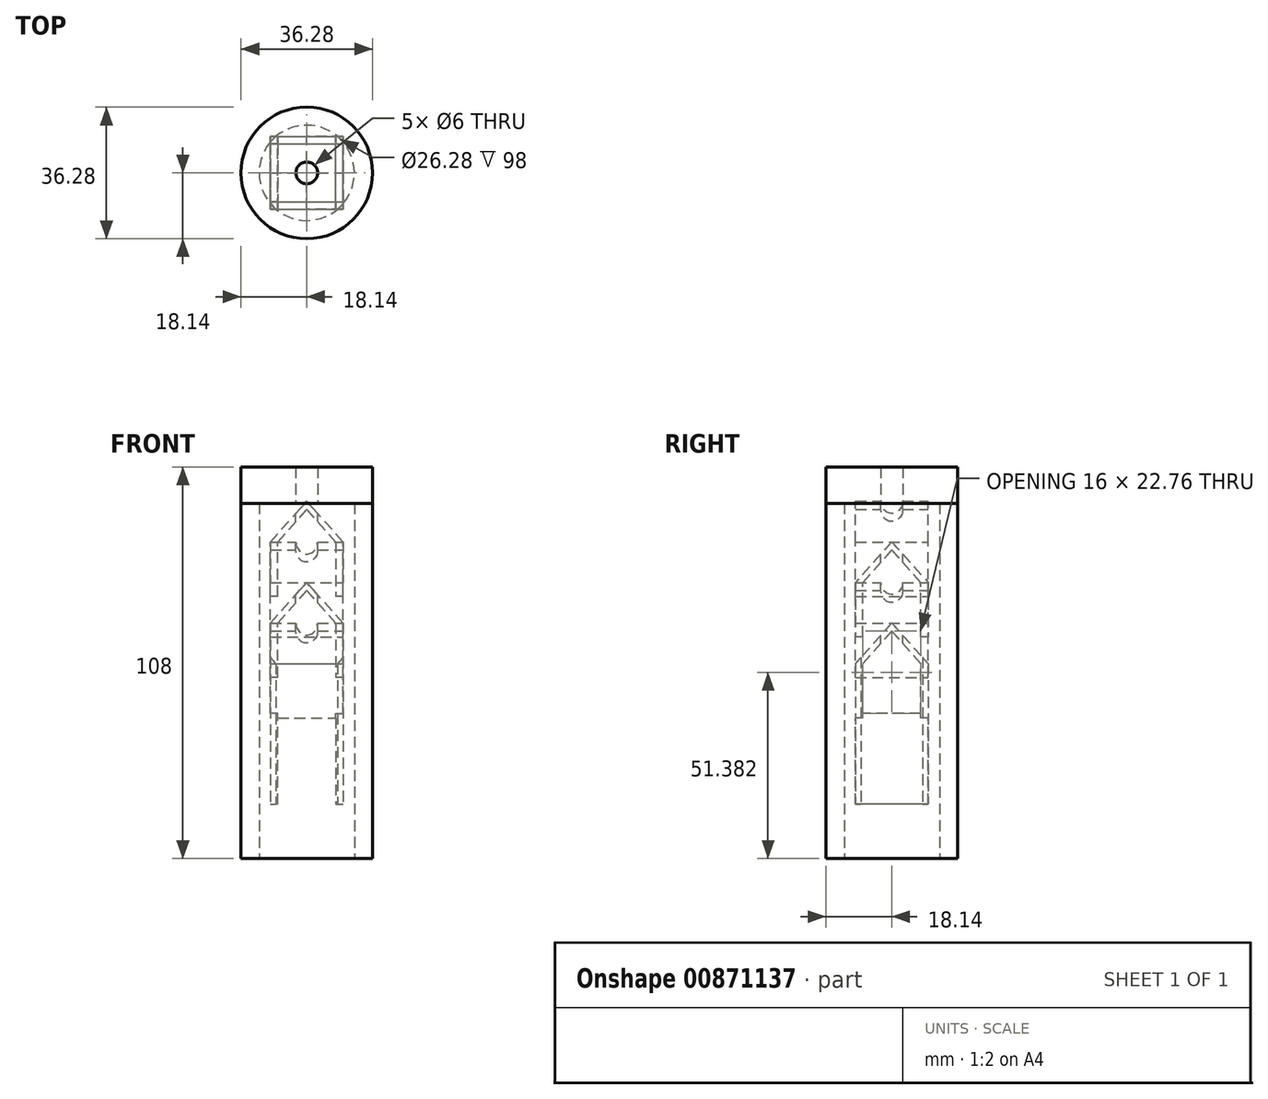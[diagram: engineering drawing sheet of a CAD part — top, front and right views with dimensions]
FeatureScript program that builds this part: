
annotation { "Feature Type Name" : "Feature", "Feature Type Description" : "" }
export const myFeature = defineFeature(function(context is Context, id is Id, definition is map)
    precondition{}
    {
        {
            var Q0;
            Q0=qCreatedBy(makeId("Front.planeOp"),FACE);
            var sketch = newSketch(context, id + "F0", { "sketchPlane" : qUnion([Q0])});
            skLineSegment(sketch, "E0", {"start": v(-10, 0) * mm, "end": v(-10, 15) * mm});
            skLineSegment(sketch, "E1", {"start": v(-10, 15) * mm, "end": v(0, 26.18) * mm});
            skLineSegment(sketch, "E2", {"start": v(0, 0) * mm, "end": v(0, 43.3) * mm, "construction": true});
            skLineSegment(sketch, "E3.MirrorCS", {"start": v(10, 15) * mm, "end": v(0, 26.18) * mm});
            skLineSegment(sketch, "E4.MirrorCS", {"start": v(10, 0) * mm, "end": v(10, 15) * mm});
            skLineSegment(sketch, "E5", {"start": v(-8, 0) * mm, "end": v(-8, 15) * mm});
            skLineSegment(sketch, "E6", {"start": v(-8, 15) * mm, "end": v(0, 23.94) * mm});
            skLineSegment(sketch, "E7", {"start": v(0, 23.94) * mm, "end": v(8, 15) * mm});
            skLineSegment(sketch, "E8", {"start": v(8, 15) * mm, "end": v(8, 0) * mm});
            skLineSegment(sketch, "E9", {"start": v(10, 15) * mm, "end": v(-10, 15) * mm, "construction": true});
            skLineSegment(sketch, "E10", {"start": v(10, 0) * mm, "end": v(8, 0) * mm});
            skLineSegment(sketch, "E11", {"start": v(-8, 0) * mm, "end": v(-10, 0) * mm});
            skLineSegment(sketch, "E12.1.0.0", {"start": v(-8, -7.36) * mm, "end": v(0, 1.58) * mm});
            skLineSegment(sketch, "E12.1.0.1", {"start": v(-10, -7.36) * mm, "end": v(0, 3.82) * mm});
            skLineSegment(sketch, "E12.1.0.2", {"start": v(10, -7.36) * mm, "end": v(0, 3.82) * mm});
            skLineSegment(sketch, "E12.1.0.3", {"start": v(0, 1.58) * mm, "end": v(8, -7.36) * mm});
            skLineSegment(sketch, "E12.1.0.4", {"start": v(8, -7.36) * mm, "end": v(8, -22.36) * mm});
            skLineSegment(sketch, "E12.1.0.5", {"start": v(10, -22.36) * mm, "end": v(10, -7.36) * mm});
            skLineSegment(sketch, "E12.1.0.6", {"start": v(-8, -22.36) * mm, "end": v(-8, -7.36) * mm});
            skLineSegment(sketch, "E12.1.0.7", {"start": v(-10, -22.36) * mm, "end": v(-10, -7.36) * mm});
            skLineSegment(sketch, "E12.1.0.8", {"start": v(-8, -22.36) * mm, "end": v(-10, -22.36) * mm});
            skLineSegment(sketch, "E12.1.0.9", {"start": v(10, -22.36) * mm, "end": v(8, -22.36) * mm});
            skLineSegment(sketch, "E12.direction1", {"start": v(-8, 15) * mm, "end": v(-8, -13.7) * mm, "construction": true});
            skLineSegment(sketch, "E13", {"start": v(-10, -22.36) * mm, "end": v(10, -22.36) * mm, "construction": true});
            skSolve(sketch);
        }
        {
            var Q0;
            Q0=qCreatedBy(makeId("Right.planeOp"),FACE);
            var sketch = newSketch(context, id + "F1", { "sketchPlane" : qUnion([Q0])});
            skLineSegment(sketch, "E14", {"start": v(0, 15) * mm, "end": v(-10, 3.82) * mm});
            skLineSegment(sketch, "E15", {"start": v(-10, 3.82) * mm, "end": v(-10, -11.18) * mm});
            skLineSegment(sketch, "E16", {"start": v(-8, -11.18) * mm, "end": v(-8, 3.82) * mm});
            skLineSegment(sketch, "E17", {"start": v(-8, 3.82) * mm, "end": v(0, 12.76) * mm});
            skLineSegment(sketch, "E18.MirrorCS", {"start": v(8, 3.82) * mm, "end": v(0, 12.76) * mm});
            skLineSegment(sketch, "E19.MirrorCS", {"start": v(0, 15) * mm, "end": v(10, 3.82) * mm});
            skLineSegment(sketch, "E20.MirrorCS", {"start": v(8, -11.18) * mm, "end": v(8, 3.82) * mm});
            skLineSegment(sketch, "E21.MirrorCS", {"start": v(10, 3.82) * mm, "end": v(10, -11.18) * mm});
            skLineSegment(sketch, "E22", {"start": v(10, 3.82) * mm, "end": v(-10, 3.82) * mm, "construction": true});
            skLineSegment(sketch, "E23", {"start": v(10, -11.18) * mm, "end": v(8, -11.18) * mm});
            skLineSegment(sketch, "E24", {"start": v(-8, -11.18) * mm, "end": v(-10, -11.18) * mm});
            skLineSegment(sketch, "E25.1.0.0", {"start": v(0, -7.36) * mm, "end": v(10, -18.54) * mm});
            skLineSegment(sketch, "E25.1.0.1", {"start": v(8, -18.54) * mm, "end": v(0, -9.6) * mm});
            skLineSegment(sketch, "E25.1.0.2", {"start": v(8, -33.54) * mm, "end": v(8, -18.54) * mm});
            skLineSegment(sketch, "E25.1.0.3", {"start": v(10, -18.54) * mm, "end": v(10, -33.54) * mm});
            skLineSegment(sketch, "E25.1.0.4", {"start": v(10, -33.54) * mm, "end": v(8, -33.54) * mm});
            skLineSegment(sketch, "E25.1.0.5", {"start": v(-8, -33.54) * mm, "end": v(-10, -33.54) * mm});
            skLineSegment(sketch, "E25.1.0.6", {"start": v(-8, -33.54) * mm, "end": v(-8, -18.54) * mm});
            skLineSegment(sketch, "E25.1.0.7", {"start": v(-10, -18.54) * mm, "end": v(-10, -33.54) * mm});
            skLineSegment(sketch, "E25.1.0.8", {"start": v(0, -7.36) * mm, "end": v(-10, -18.54) * mm});
            skLineSegment(sketch, "E25.1.0.9", {"start": v(-8, -18.54) * mm, "end": v(0, -9.6) * mm});
            skLineSegment(sketch, "E25.direction1", {"start": v(10, 3.82) * mm, "end": v(10, -18.54) * mm, "construction": true});
            skSolve(sketch);
        }
        {
            var Q0;
            Q0=makeQuery(id+"F0.imprint","IMPRINT",FACE,{"disambiguationData":[TD([[makeQuery(id+"F0.imprint","IMPRINT",EDGE,{"derivedFrom":sQuery(id+"F0.wireOp",EDGE,"E0")}),-1.0]])]});
            var Q1;
            Q1=makeQuery(id+"F0.imprint","IMPRINT",FACE,{"disambiguationData":[TD([[makeQuery(id+"F0.imprint","IMPRINT",EDGE,{"derivedFrom":sQuery(id+"F0.wireOp",EDGE,"E12.1.0.0")}),1.0]])]});
            extrude(context, id + "F2", {"entities" : qUnion([Q0, Q1]), "endBound" : BoundingType.SYMMETRIC, "depth" : 20 * mm, "offsetDistance" : 25 * mm});
        }
        {
            var Q0;
            Q0 = qSketchRegion(id + "F1", true);
            extrude(context, id + "F3", {"entities" : qUnion([Q0]), "endBound" : BoundingType.SYMMETRIC, "oppositeDirection" : true, "depth" : 20 * mm, "offsetDistance" : 25 * mm});
        }
        {
            var Q0;
            Q0=makeQuery(id+"F3.opExtrude","CAP_FACE",FACE,{"disambiguationData":[OSD([sQuery(id+"F1.wireOp",EDGE,"E25.1.0.0"),sQuery(id+"F1.wireOp",EDGE,"E25.1.0.1"),sQuery(id+"F1.wireOp",EDGE,"E25.1.0.2"),sQuery(id+"F1.wireOp",EDGE,"E25.1.0.3"),sQuery(id+"F1.wireOp",EDGE,"E25.1.0.4"),sQuery(id+"F1.wireOp",EDGE,"E25.1.0.5"),sQuery(id+"F1.wireOp",EDGE,"E25.1.0.6"),sQuery(id+"F1.wireOp",EDGE,"E25.1.0.7"),sQuery(id+"F1.wireOp",EDGE,"E25.1.0.8"),sQuery(id+"F1.wireOp",EDGE,"E25.1.0.9")])],"isStart":true});
            var sketch = newSketch(context, id + "F4", { "sketchPlane" : qUnion([Q0])});
            skLineSegment(sketch, "E26", {"start": v(-10, -32.36) * mm, "end": v(10, -32.36) * mm});
            skLineSegment(sketch, "E27", {"start": v(-10, -32.36) * mm, "end": v(-10, -57.36) * mm});
            skLineSegment(sketch, "E28", {"start": v(-10, -57.36) * mm, "end": v(10, -57.36) * mm});
            skLineSegment(sketch, "E29", {"start": v(10, -57.36) * mm, "end": v(10, -32.36) * mm});
            skSolve(sketch);
        }
        {
            var Q0;
            Q0=makeQuery(id+"F3.opExtrude","CAP_FACE",FACE,{"disambiguationData":[OSD([sQuery(id+"F1.wireOp",EDGE,"E25.1.0.0"),sQuery(id+"F1.wireOp",EDGE,"E25.1.0.1"),sQuery(id+"F1.wireOp",EDGE,"E25.1.0.2"),sQuery(id+"F1.wireOp",EDGE,"E25.1.0.3"),sQuery(id+"F1.wireOp",EDGE,"E25.1.0.4"),sQuery(id+"F1.wireOp",EDGE,"E25.1.0.5"),sQuery(id+"F1.wireOp",EDGE,"E25.1.0.6"),sQuery(id+"F1.wireOp",EDGE,"E25.1.0.7"),sQuery(id+"F1.wireOp",EDGE,"E25.1.0.8"),sQuery(id+"F1.wireOp",EDGE,"E25.1.0.9")])],"isStart":false});
            var sketch = newSketch(context, id + "F5", { "sketchPlane" : qUnion([Q0])});
            skLineSegment(sketch, "E30", {"start": v(-10, -32.36) * mm, "end": v(10, -32.36) * mm});
            skLineSegment(sketch, "E31", {"start": v(-10, -32.36) * mm, "end": v(-10, -57.36) * mm});
            skLineSegment(sketch, "E32", {"start": v(-10, -57.36) * mm, "end": v(10, -57.36) * mm});
            skLineSegment(sketch, "E33", {"start": v(10, -57.36) * mm, "end": v(10, -32.36) * mm});
            skSolve(sketch);
        }
        {
            var Q0;
            {var subQ0=sQuery(id+"F5.wireOp",EDGE,"E32");Q0=makeQuery(id+"F5.imprint","IMPRINT",FACE,{"disambiguationData":[TD([[makeQuery(id+"F5.imprint","IMPRINT",EDGE,{"derivedFrom":subQ0}),1.0]])]});}
            extrude(context, id + "F6", {"entities" : qUnion([Q0]), "operationType" : NewBodyOperationType.ADD, "oppositeDirection" : true, "depth" : 2 * mm, "offsetDistance" : 25 * mm});
        }
        {
            var Q0;
            {var subQ0=sQuery(id+"F4.wireOp",EDGE,"E28");Q0=makeQuery(id+"F4.imprint","IMPRINT",FACE,{"disambiguationData":[TD([[makeQuery(id+"F4.imprint","IMPRINT",EDGE,{"derivedFrom":subQ0}),1.0]])]});}
            extrude(context, id + "F7", {"entities" : qUnion([Q0]), "operationType" : NewBodyOperationType.ADD, "oppositeDirection" : true, "depth" : 2 * mm, "offsetDistance" : 25 * mm});
        }
        {
            var Q0;
            Q0=qCreatedBy(makeId("Top.planeOp"),FACE);
            var sketch = newSketch(context, id + "F8", { "sketchPlane" : qUnion([Q0])});
            skCircle(sketch, "E34", {"center": v(0, 0) * mm, "radius": 3 * mm});
            skSolve(sketch);
        }
        {
            var Q0;
            Q0 = qSketchRegion(id + "F8", true);
            extrude(context, id + "F9", {"entities" : qUnion([Q0]), "operationType" : NewBodyOperationType.REMOVE, "endBound" : BoundingType.SYMMETRIC, "oppositeDirection" : true, "depth" : 100 * mm, "offsetDistance" : 25 * mm});
        }
        {
            var Q0;
            Q0=makeQuery(id+"F6.opExtrude","SWEPT_FACE",FACE,{"disambiguationData":[OSD([sQuery(id+"F5.wireOp",EDGE,"E32")])]});
            var sketch = newSketch(context, id + "F10", { "sketchPlane" : qUnion([Q0])});
            skCircle(sketch, "E35", {"center": v(0, 0) * mm, "radius": 13.14 * mm});
            skCircle(sketch, "E36", {"center": v(0, 0) * mm, "radius": 18.14 * mm});
            skSolve(sketch);
        }
        {
            var Q0;
            Q0 = qSketchRegion(id + "F10", true);
            var Q1;
            Q1=makeQuery(id+"F2.opExtrude","SWEPT_FACE",FACE,{"disambiguationData":[OSD([sQuery(id+"F0.wireOp",EDGE,"E3.MirrorCS")])]});
            extrude(context, id + "F11", {"entities" : qUnion([Q0]), "oppositeDirection" : true, "depth" : 83 * mm, "endBoundEntityFace" : qUnion([Q1]), "offsetDistance" : 25 * mm});
        }
        {
            var Q0;
            Q0=makeQuery(id+"F11.opExtrude","CAP_FACE",FACE,{"disambiguationData":[OSD([sQuery(id+"F10.wireOp",EDGE,"E35"),sQuery(id+"F10.wireOp",EDGE,"E36")])],"isStart":false});
            var sketch = newSketch(context, id + "F12", { "sketchPlane" : qUnion([Q0])});
            skCircle(sketch, "E37.0", {"center": v(0, 0) * mm, "radius": 18.14 * mm});
            skArc(sketch, "E38.0", {"start": v(0, 3) * mm, "mid": v(-3, 0) * mm, "end": v(0, -3) * mm});
            skArc(sketch, "E38.1", {"start": v(0, 3) * mm, "mid": v(3, 0) * mm, "end": v(0, -3) * mm});
            skSolve(sketch);
        }
        {
            var Q0;
            Q0 = qSketchRegion(id + "F12", true);
            extrude(context, id + "F13", {"entities" : qUnion([Q0]), "depth" : 10 * mm, "offsetDistance" : 25 * mm});
        }
        {
            var Q0;
            Q0=makeQuery(id+"F11.opExtrude","CAP_FACE",FACE,{"disambiguationData":[OSD([sQuery(id+"F10.wireOp",EDGE,"E35"),sQuery(id+"F10.wireOp",EDGE,"E36")])],"isStart":true});
            var sketch = newSketch(context, id + "F14", { "sketchPlane" : qUnion([Q0])});
            skCircle(sketch, "E39.0", {"center": v(0, 0) * mm, "radius": 18.14 * mm});
            skCircle(sketch, "E39.1", {"center": v(0, 0) * mm, "radius": 13.14 * mm});
            skSolve(sketch);
        }
        {
            var Q0;
            Q0 = qSketchRegion(id + "F14", true);
            extrude(context, id + "F15", {"entities" : qUnion([Q0]), "operationType" : NewBodyOperationType.ADD, "depth" : 15 * mm, "offsetDistance" : 25 * mm});
        }
    });
